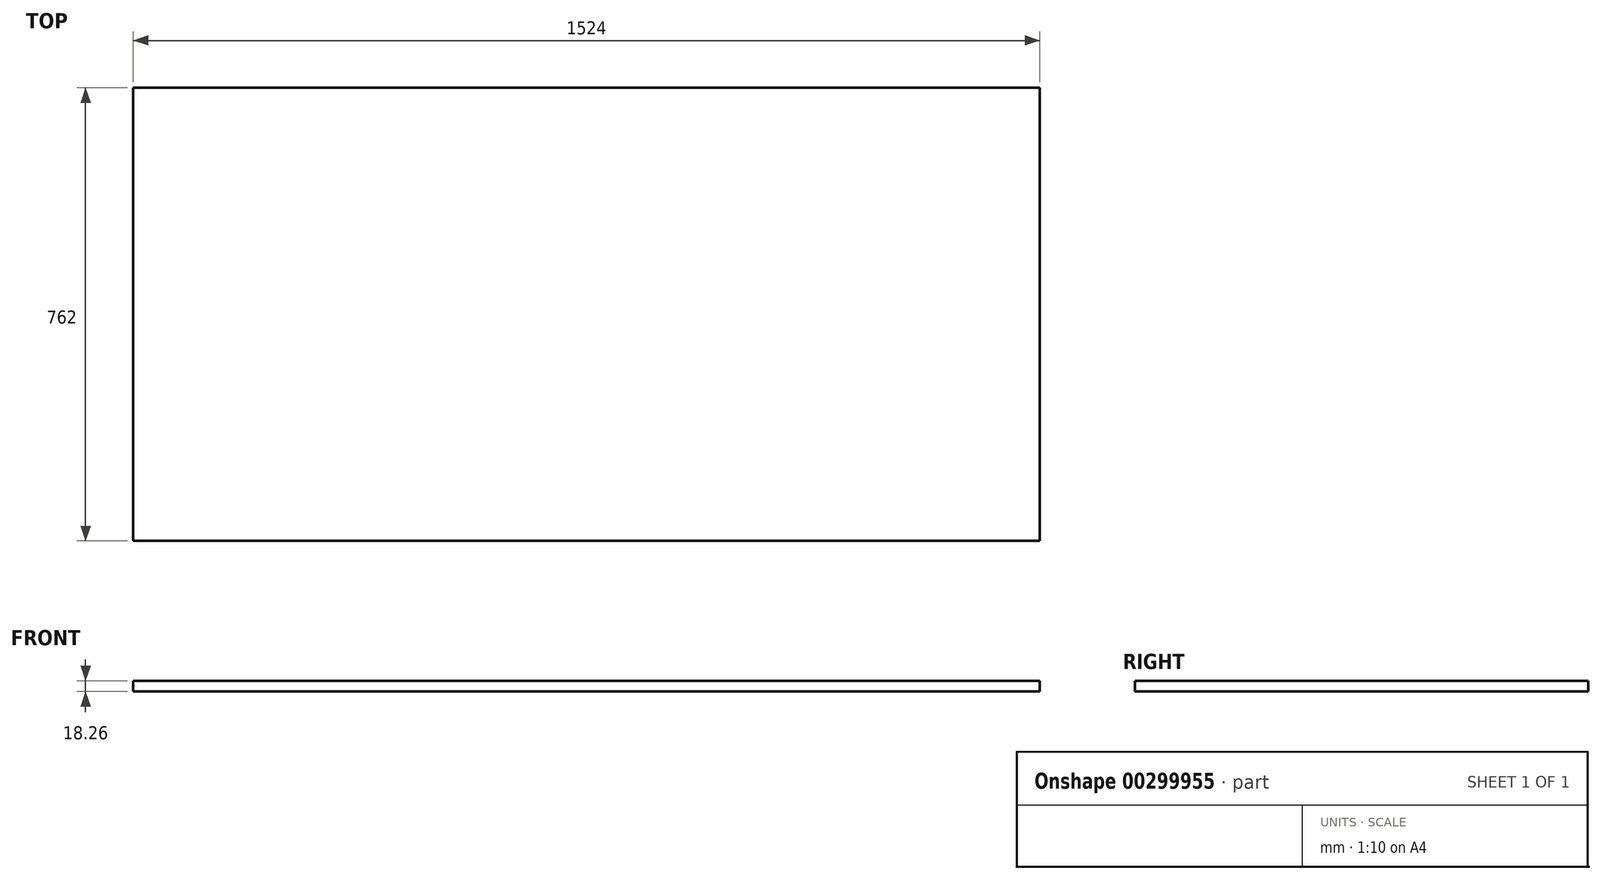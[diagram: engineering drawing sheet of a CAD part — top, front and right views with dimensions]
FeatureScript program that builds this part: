
annotation { "Feature Type Name" : "Feature", "Feature Type Description" : "" }
export const myFeature = defineFeature(function(context is Context, id is Id, definition is map)
    precondition{}
    {
        {
            var Q0;
            Q0=qCreatedBy(makeId("Top.planeOp"),FACE);
            var sketch = newSketch(context, id + "F0", { "sketchPlane" : qUnion([Q0])});
            skLineSegment(sketch, "E0.bottom", {"start": v(762, -381) * mm, "end": v(-762, -381) * mm});
            skLineSegment(sketch, "E0.top", {"start": v(762, 381) * mm, "end": v(-762, 381) * mm});
            skLineSegment(sketch, "E0.left", {"start": v(762, -381) * mm, "end": v(762, 381) * mm});
            skLineSegment(sketch, "E0.right", {"start": v(-762, -381) * mm, "end": v(-762, 381) * mm});
            skPoint(sketch, "E0.middle", {"position": v(0, 0) * mm});
            skSolve(sketch);
        }
        {
            var Q0;
            Q0=makeQuery(id+"F0.imprint","IMPRINT",FACE,{"disambiguationData":[TD([[makeQuery(id+"F0.imprint","IMPRINT",EDGE,{"derivedFrom":sQuery(id+"F0.wireOp",EDGE,"E0.bottom")}),-1.0]])]});
            extrude(context, id + "F1", {"entities" : qUnion([Q0]), "oppositeDirection" : true, "depth" : 18.26 * mm});
        }
    });
